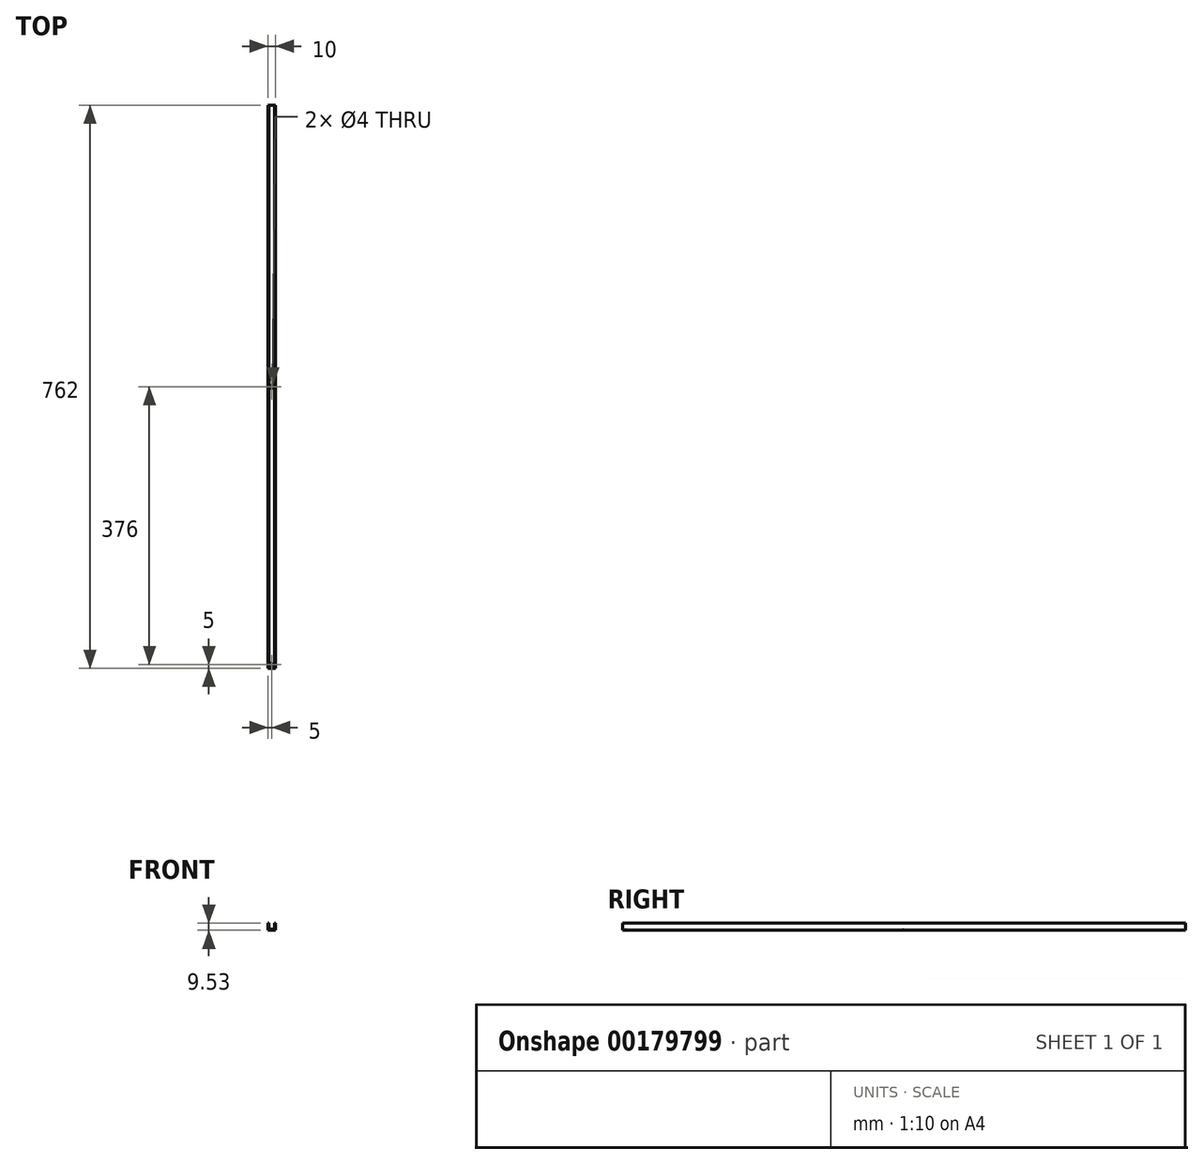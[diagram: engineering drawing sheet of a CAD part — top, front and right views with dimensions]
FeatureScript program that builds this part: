
annotation { "Feature Type Name" : "Feature", "Feature Type Description" : "" }
export const myFeature = defineFeature(function(context is Context, id is Id, definition is map)
    precondition{}
    {
        {
            var Q0;
            Q0=qCreatedBy(makeId("Front.planeOp"),FACE);
            var sketch = newSketch(context, id + "F0", { "sketchPlane" : qUnion([Q0])});
            skLineSegment(sketch, "E0", {"start": v(-5, 9.52) * mm, "end": v(-5, 0) * mm});
            skLineSegment(sketch, "E1", {"start": v(-5, 0) * mm, "end": v(0, 0) * mm});
            skLineSegment(sketch, "E2.MirrorCS", {"start": v(5, 9.52) * mm, "end": v(5, 0) * mm});
            skLineSegment(sketch, "E3.MirrorCS", {"start": v(5, 0) * mm, "end": v(0, 0) * mm});
            skLineSegment(sketch, "E4", {"start": v(-3.8, 9.52) * mm, "end": v(-3.8, 1.2) * mm});
            skLineSegment(sketch, "E5", {"start": v(-3.8, 1.2) * mm, "end": v(3.8, 1.2) * mm});
            skLineSegment(sketch, "E6", {"start": v(3.8, 1.2) * mm, "end": v(3.8, 9.52) * mm});
            skPoint(sketch, "E7.visualSharp", {"position": v(3.8, 9.53) * mm});
            skPoint(sketch, "E8.visualSharp", {"position": v(5, 9.4) * mm});
            skLineSegment(sketch, "E9", {"start": v(-5, 9.52) * mm, "end": v(-3.8, 9.52) * mm});
            skLineSegment(sketch, "E10", {"start": v(3.8, 9.52) * mm, "end": v(5, 9.52) * mm});
            skSolve(sketch);
        }
        {
            var Q0;
            Q0 = qSketchRegion(id + "F0", true);
            extrude(context, id + "F1", {"entities" : qUnion([Q0]), "depth" : 381 * mm, "hasSecondDirection" : true, "secondDirectionOppositeDirection" : true, "secondDirectionDepth" : 381 * mm});
        }
        {
            var Q0;
            Q0=makeQuery(id+"F1.opExtrude","SWEPT_FACE",FACE,{"disambiguationData":[OSD([sQuery(id+"F0.wireOp",EDGE,"E1"),sQuery(id+"F0.wireOp",EDGE,"E3.MirrorCS")])]});
            var sketch = newSketch(context, id + "F2", { "sketchPlane" : qUnion([Q0])});
            skCircle(sketch, "E11", {"center": v(0, 0) * mm, "radius": 2 * mm});
            skSolve(sketch);
        }
        {
            var Q0;
            Q0=makeQuery(id+"F2.imprint","IMPRINT",FACE,{"disambiguationData":[TD([[makeQuery(id+"F2.imprint","IMPRINT",EDGE,{"derivedFrom":sQuery(id+"F2.wireOp",EDGE,"E11")}),1.0]])]});
            extrude(context, id + "F3", {"entities" : qUnion([Q0]), "operationType" : NewBodyOperationType.REMOVE, "endBound" : BoundingType.UP_TO_NEXT, "oppositeDirection" : true, "depth" : 25 * mm});
        }
        {
            var Q0;
            Q0=makeQuery(id+"F1.opExtrude","SWEPT_FACE",FACE,{"disambiguationData":[OSD([sQuery(id+"F0.wireOp",EDGE,"E1"),sQuery(id+"F0.wireOp",EDGE,"E3.MirrorCS")])]});
            var sketch = newSketch(context, id + "F4", { "sketchPlane" : qUnion([Q0])});
            skLineSegment(sketch, "E12", {"start": v(-5, 376) * mm, "end": v(-5, 381) * mm});
            skLineSegment(sketch, "E13", {"start": v(-5, 381) * mm, "end": v(5, 381) * mm});
            skLineSegment(sketch, "E14", {"start": v(5, 381) * mm, "end": v(5, 376) * mm});
            skCircle(sketch, "E15", {"center": v(0, 376) * mm, "radius": 2 * mm});
            skSolve(sketch);
        }
        {
            var Q0;
            Q0 = qSketchRegion(id + "F4", true);
            extrude(context, id + "F5", {"entities" : qUnion([Q0]), "operationType" : NewBodyOperationType.REMOVE, "endBound" : BoundingType.THROUGH_ALL, "oppositeDirection" : true, "depth" : 25 * mm});
        }
    });
